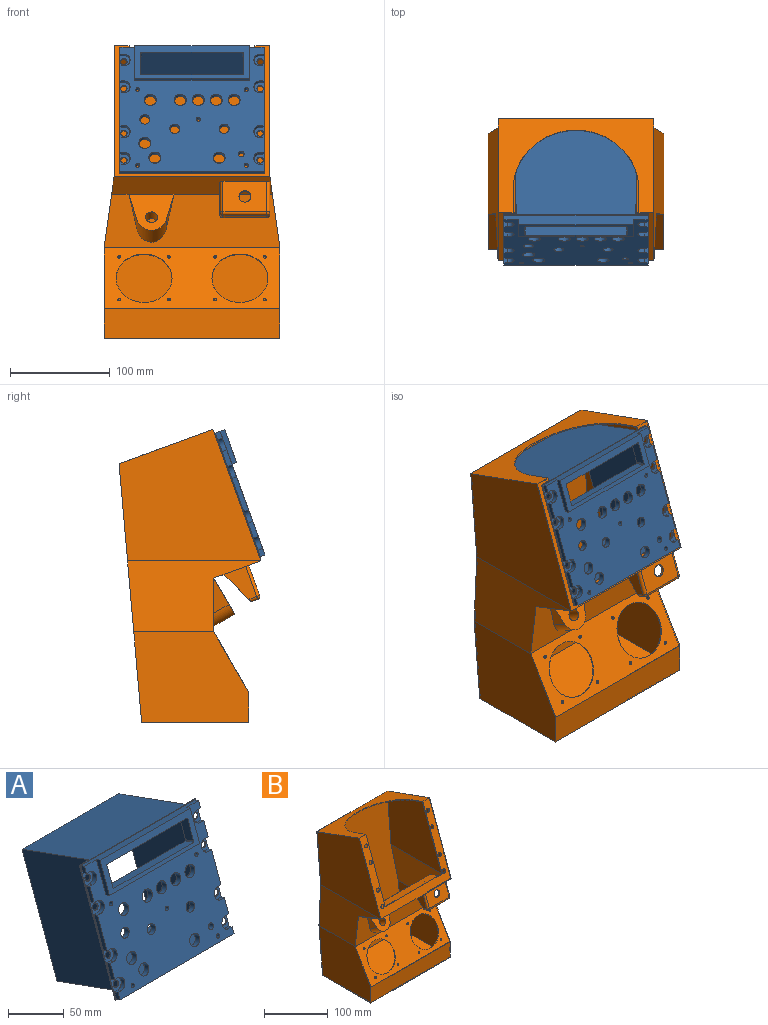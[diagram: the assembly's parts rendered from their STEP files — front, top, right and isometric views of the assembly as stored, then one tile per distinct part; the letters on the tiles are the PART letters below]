
ASSEMBLY  parts=2 mates=3
PART A: 89 faces, bbox 146x135.5x156.3 mm
  f0: plane 144.4x123.81mm, normal (0,-0.94,0.34), area 12879.8mm2, adj f7,f8,f9,f10,f11,f12,f13,f14
  f1: plane 146x125.31mm, normal (0,0.94,-0.34), area 3302.6mm2, adj f3,f4,f5,f6,f43,f44,f45,f46
  f2: plane 146x125.31mm, normal (0,-0.94,0.34), area 1089.9mm2, adj f3,f4,f5,f6,f7,f8,f9,f10
  f3: plane 146x85.51mm, normal (0,0.34,0.94), area 11126mm2, adj f1,f2,f4,f6,f51,f52,f58
  f4: plane 125.65x46.55mm, normal (-1,0,0), area 133.4mm2, adj f1,f2,f3,f5
  f5: plane 146x0.94mm, normal (0,-0.34,-0.94), area 146mm2, adj f1,f2,f4,f6
  f6: plane 125.65x46.55mm, normal (1,0,0), area 133.4mm2, adj f1,f2,f3,f5
  f7: plane 8.42x7.14mm, normal (-1,0,0), area 35.7mm2, adj f0,f2,f8,f42
  f8: plane 144.4x4.7mm, normal (0,-0.34,-0.94), area 722mm2, adj f0,f2,f7,f9
  f9: plane 8.42x7.14mm, normal (1,0,0), area 35.7mm2, adj f0,f2,f8,f10
  f10: plane 4.7x3.96mm, normal (0,0.34,0.94), area 19.8mm2, adj f0,f2,f9,f11
  f11: cylinder r=6.35mm len=13.64mm, axis (0,0.94,-0.34), area 99.7mm2, adj f0,f2,f10,f12
  f12: plane 4.7x3.96mm, normal (0,-0.34,-0.94), area 19.8mm2, adj f0,f2,f11,f13
  f13: plane 16.63x10.13mm, normal (1,0,0), area 79.4mm2, adj f0,f2,f12,f14
  f14: plane 4.7x3.96mm, normal (0,0.34,0.94), area 19.8mm2, adj f0,f2,f13,f15
  f15: cylinder r=6.35mm len=13.64mm, axis (0,0.94,-0.34), area 99.7mm2, adj f0,f2,f14,f16
  f16: plane 4.7x3.96mm, normal (0,-0.34,-0.94), area 19.8mm2, adj f0,f2,f15,f17
  f17: plane 34.53x16.64mm, normal (1,0,0), area 174.6mm2, adj f0,f2,f16,f18
  f18: plane 4.7x3.96mm, normal (0,0.34,0.94), area 19.8mm2, adj f0,f2,f17,f19
  f19: cylinder r=6.35mm len=13.64mm, axis (0,0.94,-0.34), area 99.7mm2, adj f0,f2,f18,f20
  f20: plane 4.7x3.96mm, normal (0,-0.34,-0.94), area 19.8mm2, adj f0,f2,f19,f21
  f21: plane 16.63x10.13mm, normal (1,0,0), area 79.4mm2, adj f0,f2,f20,f22
  f22: plane 4.7x3.96mm, normal (0,0.34,0.94), area 19.8mm2, adj f0,f2,f21,f23
  f23: cylinder r=6.35mm len=13.64mm, axis (0,0.94,-0.34), area 99.7mm2, adj f0,f2,f22,f24
  f24: plane 4.7x3.96mm, normal (0,-0.34,-0.94), area 19.8mm2, adj f0,f2,f23,f25
  f25: plane 8.42x7.14mm, normal (1,0,0), area 35.7mm2, adj f0,f2,f24,f26
  f26: plane 144.4x9.4mm, normal (0,0.34,0.94), area 1294mm2, adj f0,f2,f25,f27,f77,f78,f80
  f27: plane 8.42x7.14mm, normal (-1,0,0), area 35.7mm2, adj f0,f2,f26,f28
  f28: plane 4.7x3.96mm, normal (0,-0.34,-0.94), area 19.8mm2, adj f0,f2,f27,f29
  f29: cylinder r=6.35mm len=13.64mm, axis (0,0.94,-0.34), area 99.7mm2, adj f0,f2,f28,f30
  f30: plane 4.7x3.96mm, normal (0,0.34,0.94), area 19.8mm2, adj f0,f2,f29,f31
  f31: plane 16.63x10.13mm, normal (-1,0,0), area 79.4mm2, adj f0,f2,f30,f32
  f32: plane 4.7x3.96mm, normal (0,-0.34,-0.94), area 19.8mm2, adj f0,f2,f31,f33
  f33: cylinder r=6.35mm len=13.64mm, axis (0,0.94,-0.34), area 99.7mm2, adj f0,f2,f32,f34
  f34: plane 4.7x3.96mm, normal (0,0.34,0.94), area 19.8mm2, adj f0,f2,f33,f35
  f35: plane 34.53x16.64mm, normal (-1,0,0), area 174.6mm2, adj f0,f2,f34,f36
  f36: plane 4.7x3.96mm, normal (0,-0.34,-0.94), area 19.8mm2, adj f0,f2,f35,f37
  f37: cylinder r=6.35mm len=13.64mm, axis (0,0.94,-0.34), area 99.7mm2, adj f0,f2,f36,f38
  f38: plane 4.7x3.96mm, normal (0,0.34,0.94), area 19.8mm2, adj f0,f2,f37,f39
  f39: plane 16.63x10.13mm, normal (-1,0,0), area 79.4mm2, adj f0,f2,f38,f40
  f40: plane 4.7x3.96mm, normal (0,-0.34,-0.94), area 19.8mm2, adj f0,f2,f39,f41
  f41: cylinder r=6.35mm len=13.64mm, axis (0,0.94,-0.34), area 99.7mm2, adj f0,f2,f40,f42
  f42: plane 4.7x3.96mm, normal (0,0.34,0.94), area 19.8mm2, adj f0,f2,f7,f41
  f43: cylinder r=3.24mm len=6.48mm, axis (0,-0.94,0.34), area 20.4mm2, adj f1,f2
  f44: cylinder r=3.24mm len=6.48mm, axis (0,-0.94,0.34), area 20.4mm2, adj f1,f2
  f45: cylinder r=3.24mm len=6.48mm, axis (0,-0.94,0.34), area 20.4mm2, adj f1,f2
  f46: cylinder r=3.24mm len=6.48mm, axis (0,-0.94,0.34), area 20.4mm2, adj f1,f2
  f47: cylinder r=3.24mm len=6.48mm, axis (0,-0.94,0.34), area 20.4mm2, adj f1,f2
  f48: cylinder r=3.24mm len=6.48mm, axis (0,-0.94,0.34), area 20.4mm2, adj f1,f2
  f49: cylinder r=3.24mm len=6.48mm, axis (0,-0.94,0.34), area 20.4mm2, adj f1,f2
  f50: cylinder r=3.24mm len=6.48mm, axis (0,-0.94,0.34), area 20.4mm2, adj f1,f2
  f51: plane 153.27x129.15mm, normal (-1,0,0), area 11731.5mm2, adj f1,f3,f57,f58
  f52: plane 153.27x129.15mm, normal (1,0,0), area 11731.5mm2, adj f1,f3,f57,f58
  f53: plane 120x84.57mm, normal (0,0.34,0.94), area 10800mm2, adj f54,f56,f58,f59
  f54: plane 151.39x128.47mm, normal (-1,0,0), area 11551.5mm2, adj f53,f55,f58,f59
  f55: plane 120x84.57mm, normal (0,-0.34,-0.94), area 10800mm2, adj f54,f56,f58,f59
  f56: plane 151.39x128.47mm, normal (1,0,0), area 11551.5mm2, adj f53,f55,f58,f59
  f57: plane 122x84.57mm, normal (0,-0.34,-0.94), area 10980mm2, adj f1,f51,f52,f58
  f58: plane 122.49x122mm, normal (0,0.94,-0.34), area 500.7mm2, adj f3,f51,f52,f53,f54,f55,f56,f57
  f59: plane 120.61x120mm, normal (0,0.94,-0.34), area 11713.8mm2, adj f53,f54,f55,f56,f60,f61,f62,f63
  f60: cylinder r=2mm len=7.01mm, axis (0,-0.94,0.34), area 75.4mm2, adj f0,f59
  f61: cylinder r=5mm len=11.45mm, axis (0,-0.94,0.34), area 188.5mm2, adj f0,f59
  f62: cylinder r=5mm len=11.45mm, axis (0,-0.94,0.34), area 188.5mm2, adj f0,f59
  f63: cylinder r=5mm len=11.45mm, axis (0,-0.94,0.34), area 188.5mm2, adj f0,f59
  f64: cylinder r=6mm len=13.33mm, axis (0,-0.94,0.34), area 226.2mm2, adj f0,f59
  f65: cylinder r=2mm len=7.01mm, axis (0,-0.94,0.34), area 75.4mm2, adj f0,f59
  f66: cylinder r=3mm len=7.69mm, axis (0,-0.94,0.34), area 113.1mm2, adj f0,f59
  f67: cylinder r=6mm len=13.33mm, axis (0,-0.94,0.34), area 226.2mm2, adj f0,f59
  f68: cylinder r=6mm len=13.33mm, axis (0,-0.94,0.34), area 226.2mm2, adj f0,f59
  f69: cylinder r=2mm len=7.01mm, axis (0,-0.94,0.34), area 75.4mm2, adj f0,f59
  f70: cylinder r=2mm len=7.01mm, axis (0,-0.94,0.34), area 75.4mm2, adj f0,f59
  f71: cylinder r=2mm len=7.01mm, axis (0,-0.94,0.34), area 75.4mm2, adj f0,f59
  f72: cylinder r=6mm len=13.33mm, axis (0,-0.94,0.34), area 226.2mm2, adj f0,f59
  f73: cylinder r=6mm len=13.33mm, axis (0,-0.94,0.34), area 226.2mm2, adj f0,f59
  f74: cylinder r=6mm len=13.33mm, axis (0,-0.94,0.34), area 226.2mm2, adj f0,f59
  f75: cylinder r=6mm len=13.33mm, axis (0,-0.94,0.34), area 226.2mm2, adj f0,f59
  f76: cylinder r=6mm len=13.33mm, axis (0,-0.94,0.34), area 226.2mm2, adj f0,f59
  f77: plane 34.6x16.67mm, normal (1,0,0), area 175mm2, adj f0,f26,f79,f80
  f78: plane 34.6x16.67mm, normal (-1,0,0), area 175mm2, adj f0,f26,f79,f80
  f79: plane 114.4x4.7mm, normal (0,-0.34,-0.94), area 572mm2, adj f0,f77,f78,f80
  f80: plane 114.4x32.89mm, normal (0,-0.94,0.34), area 1547.3mm2, adj f26,f77,f78,f79,f81,f82,f83,f84
  f81: cylinder r=1mm len=10.68mm, axis (0,-0.94,0.34), area 17.3mm2, adj f59,f80,f82,f88
  f82: plane 100.4x10.34mm, normal (0,0.34,0.94), area 1104.4mm2, adj f59,f80,f81,f83
  f83: cylinder r=1mm len=10.68mm, axis (0,-0.94,0.34), area 17.3mm2, adj f59,f80,f82,f84
  f84: plane 24.44x17.86mm, normal (-1,0,0), area 242mm2, adj f59,f80,f83,f85
  f85: cylinder r=1mm len=10.68mm, axis (0,-0.94,0.34), area 17.3mm2, adj f59,f80,f84,f86
  f86: plane 100.4x10.34mm, normal (0,-0.34,-0.94), area 1104.4mm2, adj f59,f80,f85,f87
  f87: cylinder r=1mm len=10.68mm, axis (0,-0.94,0.34), area 17.3mm2, adj f59,f80,f86,f88
  f88: plane 24.44x17.86mm, normal (1,0,0), area 242mm2, adj f59,f80,f81,f87
PART B: 73 faces, bbox 177.4x143.3x294.7 mm
  f0: plane 156x131.56mm, normal (0,-0.94,0.34), area 5826.2mm2, adj f1,f4,f9,f12,f15,f16,f17,f57
  f1: plane 156x93.97mm, normal (0,0.34,0.94), area 6215.5mm2, adj f0,f3,f9,f12,f15,f17,f31
  f2: plane 154x92.31mm, normal (0,-0.34,-0.94), area 5869.3mm2, adj f15,f17,f18,f19,f25,f28,f31
  f3: plane 259.01x175.97mm, normal (0,1,-0.09), area 43088.1mm2, adj f1,f8,f9,f10,f11,f12,f13,f14
  f4: plane 160.81x46.98mm, normal (0,-0.34,-0.94), area 6608mm2, adj f0,f5,f10,f13,f34,f35,f37,f38
  f5: plane 175.97x53.93mm, normal (0,-1,0), area 7499.9mm2, adj f4,f6,f10,f13,f51,f52,f53
  f6: plane 175.97x60.62mm, normal (0,-0.87,0.5), area 7335.1mm2, adj f5,f7,f11,f14,f32,f33,f65,f66
  f7: plane 175.97x30mm, normal (0,-1,0), area 5279mm2, adj f6,f8,f11,f14
  f8: plane 175.97x107.21mm, normal (0,0,-1), area 18864.8mm2, adj f3,f7,f11,f14
  f9: plane 141.85x131.56mm, normal (-1,0,0), area 13490.4mm2, adj f0,f1,f3,f10
  f10: plane 133.33x71.03mm, normal (-0.99,0,0.14), area 6376.9mm2, adj f3,f4,f5,f9,f11
  f11: plane 115.14x90.62mm, normal (-1,0,0), area 9013.6mm2, adj f3,f6,f7,f8,f10
  f12: plane 141.85x131.56mm, normal (1,0,0), area 13490.4mm2, adj f0,f1,f3,f13
  f13: plane 133.33x71.03mm, normal (0.99,0,0.14), area 6376.9mm2, adj f3,f4,f5,f12,f14
  f14: plane 115.14x90.62mm, normal (1,0,0), area 9013.6mm2, adj f3,f6,f7,f8,f13
  f15: plane 117.8x66.25mm, normal (1,0,0), area 149mm2, adj f0,f1,f2,f16,f18,f31
  f16: plane 126x0.94mm, normal (0,0.34,0.94), area 126mm2, adj f0,f15,f17,f18
  f17: plane 117.8x66.25mm, normal (-1,0,0), area 149mm2, adj f0,f1,f2,f16,f18,f31
  f18: plane 154x129.68mm, normal (0,0.94,-0.34), area 5364.2mm2, adj f2,f15,f16,f17,f20,f25,f28,f57
  f19: plane 257.33x173.97mm, normal (0,-1,0.09), area 42287.4mm2, adj f2,f24,f25,f26,f27,f28,f29,f30
  f20: plane 158.59x46.7mm, normal (0,0.34,0.94), area 7763.4mm2, adj f18,f21,f25,f26,f28,f29
  f21: plane 175.42x56.36mm, normal (0,1,0), area 8999.8mm2, adj f20,f22,f26,f27,f29,f30,f55
  f22: plane 173.97x60.62mm, normal (0,0.87,-0.5), area 7195.1mm2, adj f21,f23,f27,f30,f32,f33,f65,f66
  f23: plane 173.97x28.73mm, normal (0,1,0), area 4998.4mm2, adj f22,f24,f27,f30
  f24: plane 173.97x105.29mm, normal (0,0,1), area 18317mm2, adj f19,f23,f27,f30
  f25: plane 139.51x130.35mm, normal (1,0,0), area 13163.1mm2, adj f2,f18,f19,f20,f26
  f26: plane 129.21x71.03mm, normal (0.99,0,-0.14), area 6197mm2, adj f19,f20,f21,f25,f27
  f27: plane 113.13x89.55mm, normal (1,0,0), area 8712mm2, adj f19,f21,f22,f23,f24,f26
  f28: plane 139.51x130.35mm, normal (-1,0,0), area 13163.1mm2, adj f2,f18,f19,f20,f29
  f29: plane 129.21x71.03mm, normal (-0.99,0,-0.14), area 6197mm2, adj f19,f20,f21,f28,f30
  f30: plane 113.13x89.55mm, normal (-1,0,0), area 8712mm2, adj f19,f21,f22,f23,f24,f29
  f31: cylinder r=63mm len=126mm, axis (0,0.34,0.94), area 197.9mm2, adj f1,f2,f15,f17
  f32: cylinder r=28mm len=56mm, axis (0,-0.87,0.5), area 175.9mm2, adj f6,f22
  f33: cylinder r=28mm len=56mm, axis (0,-0.87,0.5), area 175.9mm2, adj f6,f22
  f34: plane 50.59x27.9mm, normal (0,0.71,-0.71), area 387.4mm2, adj f4,f36,f37,f38,f39,f41,f42,f43
  f35: plane 44x30.07mm, normal (0,-0.94,0.34), area 1294.9mm2, adj f4,f45,f46,f50,f56
  f36: plane 44x6.58mm, normal (0,-0.34,-0.94), area 308mm2, adj f34,f44,f47,f50
  f37: plane 32.94x32.86mm, normal (-1,0,0), area 507.5mm2, adj f4,f34,f44,f45
  f38: plane 32.94x32.86mm, normal (1,0,0), area 507.5mm2, adj f4,f34,f46,f47
  f39: plane 32.33x32.09mm, normal (-1,0,0), area 492.7mm2, adj f34,f40,f42,f43
  f40: plane 45x29.13mm, normal (0,0.94,-0.34), area 1281.9mm2, adj f39,f41,f42,f43,f56
  f41: plane 32.33x32.09mm, normal (1,0,0), area 492.7mm2, adj f34,f40,f42,f43
  f42: plane 45x21.73mm, normal (0,-0.34,-0.94), area 1040.5mm2, adj f34,f39,f40,f41
  f43: plane 45x8.14mm, normal (0,0.34,0.94), area 390mm2, adj f34,f39,f40,f41
  f44: cylinder r=3mm len=8.92mm, axis (0,-0.94,0.34), area 36.3mm2, adj f34,f36,f37,f48
  f45: cylinder r=3mm len=31.1mm, axis (0,0.34,0.94), area 150.8mm2, adj f4,f35,f37,f48
  f46: cylinder r=3mm len=31.1mm, axis (0,-0.34,-0.94), area 150.8mm2, adj f4,f35,f38,f49
  f47: cylinder r=3mm len=8.92mm, axis (0,0.94,-0.34), area 36.3mm2, adj f34,f36,f38,f49
  f48: sphere r=3mm, area 13.4mm2, adj f44,f45,f50
  f49: sphere r=3mm, area 13.4mm2, adj f46,f47,f50
  f50: cylinder r=3mm len=44mm, axis (1,0,0), area 207.3mm2, adj f35,f36,f48,f49
  f51: plane 35.23x15.25mm, normal (0.97,-0.13,-0.22), area 277.7mm2, adj f5,f53,f54
  f52: plane 35.23x15.25mm, normal (-0.97,-0.13,-0.22), area 277.7mm2, adj f5,f53,f54
  f53: cylinder r=15mm len=29.02mm, axis (0,-0.87,0.5), area 859.5mm2, adj f5,f51,f52,f54
  f54: plane 45x36.12mm, normal (0,-0.87,0.5), area 1256.7mm2, adj f4,f51,f52,f53,f55
  f55: cylinder r=6mm len=23.37mm, axis (0,-0.87,0.5), area 629.3mm2, adj f21,f54
  f56: cylinder r=6mm len=12.13mm, axis (0,-0.94,0.34), area 94.2mm2, adj f35,f40
  f57: cylinder r=3.24mm len=6.48mm, axis (0,-0.94,0.34), area 20.4mm2, adj f0,f18
  f58: cylinder r=3.24mm len=6.48mm, axis (0,-0.94,0.34), area 20.4mm2, adj f0,f18
  f59: cylinder r=3.24mm len=6.48mm, axis (0,-0.94,0.34), area 20.4mm2, adj f0,f18
  f60: cylinder r=3.24mm len=6.48mm, axis (0,-0.94,0.34), area 20.4mm2, adj f0,f18
  f61: cylinder r=3.24mm len=6.48mm, axis (0,-0.94,0.34), area 20.4mm2, adj f0,f18
  f62: cylinder r=3.24mm len=6.48mm, axis (0,-0.94,0.34), area 20.4mm2, adj f0,f18
  f63: cylinder r=3.24mm len=6.48mm, axis (0,-0.94,0.34), area 20.4mm2, adj f0,f18
  f64: cylinder r=3.24mm len=6.48mm, axis (0,-0.94,0.34), area 20.4mm2, adj f0,f18
  f65: cylinder r=1.5mm len=3.1mm, axis (0,-0.87,0.5), area 9.4mm2, adj f6,f22
  f66: cylinder r=1.5mm len=3.1mm, axis (0,-0.87,0.5), area 9.4mm2, adj f6,f22
  f67: cylinder r=1.5mm len=3.1mm, axis (0,-0.87,0.5), area 9.4mm2, adj f6,f22
  f68: cylinder r=1.5mm len=3.1mm, axis (0,-0.87,0.5), area 9.4mm2, adj f6,f22
  f69: cylinder r=1.5mm len=3.1mm, axis (0,-0.87,0.5), area 9.4mm2, adj f6,f22
  f70: cylinder r=1.5mm len=3.1mm, axis (0,-0.87,0.5), area 9.4mm2, adj f6,f22
  f71: cylinder r=1.5mm len=3.1mm, axis (0,-0.87,0.5), area 9.4mm2, adj f6,f22
  f72: cylinder r=1.5mm len=3.1mm, axis (0,-0.87,0.5), area 9.4mm2, adj f6,f22
PLACE A t=(-98.48,-94.61,50.93)mm
PLACE B t=(-98.48,-94.61,50.93)mm fixed
MATE revolute A.f23 <-> B.f64  axis (0,0.94,-0.34) through (69.76,-100.63,34.38)mm
MATE revolute A.f29 <-> B.f57  axis (0,0.94,-0.34) through (-66.71,-100.63,34.38)mm
MATE planar A.f59 <-> B.f0  axis (0,0.94,-0.34) through (1.52,-121.02,-21.64)mm
